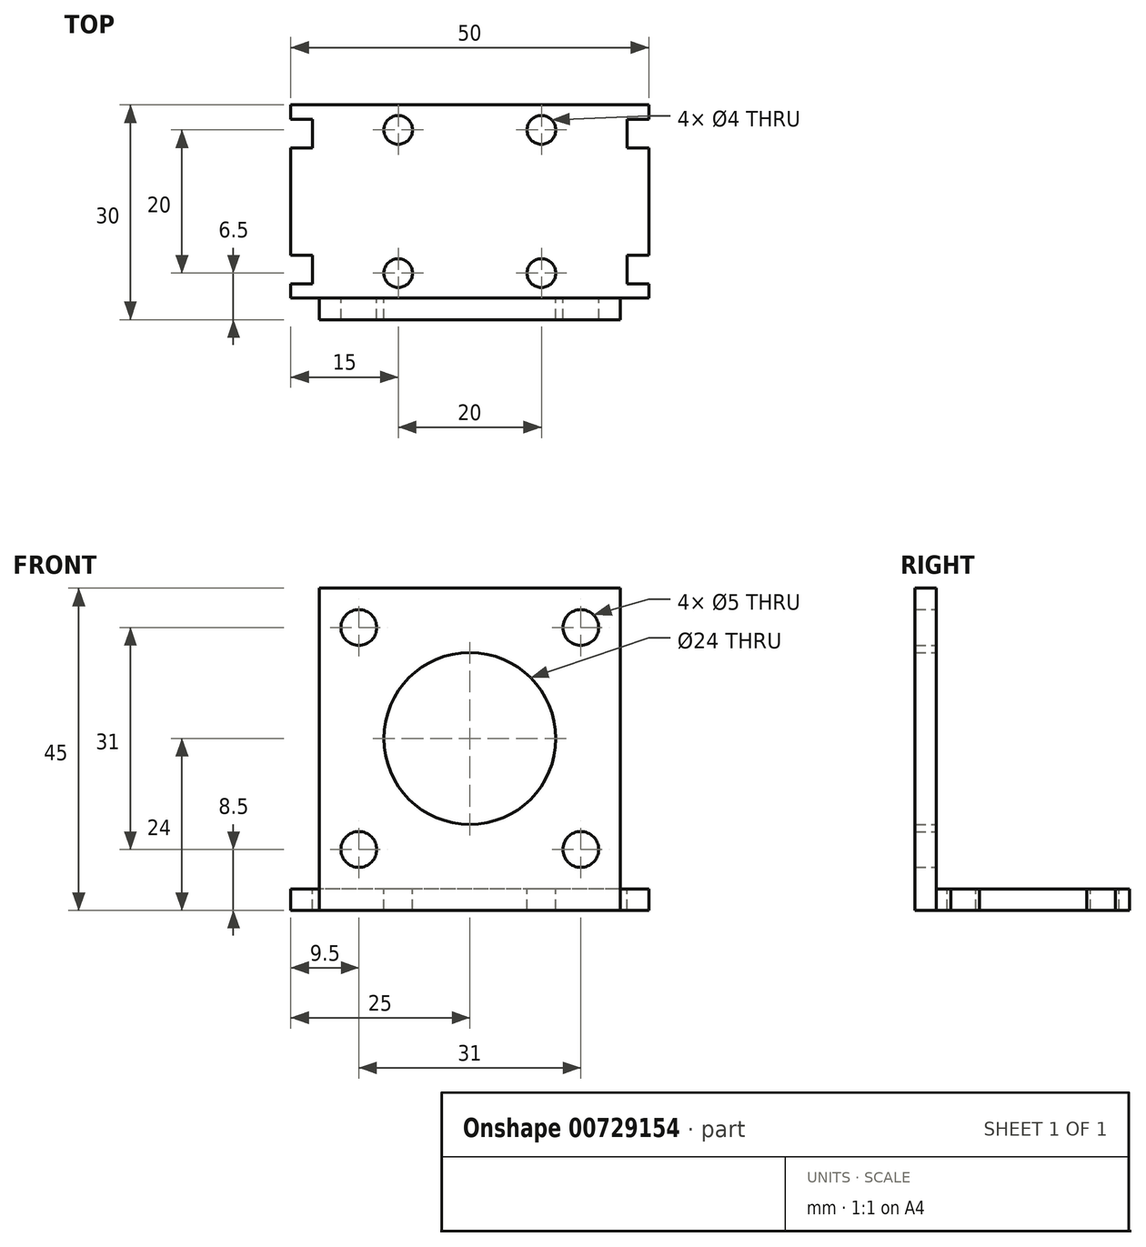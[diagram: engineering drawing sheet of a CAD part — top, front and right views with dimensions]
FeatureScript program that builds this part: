
annotation { "Feature Type Name" : "Feature", "Feature Type Description" : "" }
export const myFeature = defineFeature(function(context is Context, id is Id, definition is map)
    precondition{}
    {
        {
            var Q0;
            Q0=qCreatedBy(makeId("Top.planeOp"),FACE);
            var sketch = newSketch(context, id + "F0", { "sketchPlane" : qUnion([Q0])});
            skLineSegment(sketch, "E0.bottom", {"start": v(21, -15) * mm, "end": v(-21, -15) * mm});
            skLineSegment(sketch, "E0.top", {"start": v(21, 15) * mm, "end": v(-21, 15) * mm});
            skLineSegment(sketch, "E0.left", {"start": v(21, -15) * mm, "end": v(21, 15) * mm});
            skLineSegment(sketch, "E0.right", {"start": v(-21, -15) * mm, "end": v(-21, 15) * mm});
            skPoint(sketch, "E0.middle", {"position": v(0, 0) * mm});
            skLineSegment(sketch, "E1", {"start": v(21, -12) * mm, "end": v(-21, -12) * mm});
            skSolve(sketch);
        }
        {
            var Q0;
            {var subQ0=sQuery(id+"F0.wireOp",EDGE,"E0.top");Q0=makeQuery(id+"F0.imprint","IMPRINT",FACE,{"disambiguationData":[TD([[makeQuery(id+"F0.imprint","IMPRINT",EDGE,{"derivedFrom":subQ0}),1.0]])]});}
            extrude(context, id + "F1", {"entities" : qUnion([Q0]), "depth" : 3 * mm, "offsetDistance" : 25 * mm});
        }
        {
            var Q0;
            {var subQ0=sQuery(id+"F0.wireOp",EDGE,"E0.bottom");Q0=makeQuery(id+"F0.imprint","IMPRINT",FACE,{"disambiguationData":[TD([[makeQuery(id+"F0.imprint","IMPRINT",EDGE,{"derivedFrom":subQ0}),-1.0]])]});}
            extrude(context, id + "F2", {"entities" : qUnion([Q0]), "operationType" : NewBodyOperationType.ADD, "depth" : 45 * mm, "offsetDistance" : 25 * mm});
        }
        {
            var Q0;
            Q0=makeQuery(id+"F1.opExtrude","CAP_FACE",FACE,{"disambiguationData":[OSD([sQuery(id+"F0.wireOp",EDGE,"E0.top"),sQuery(id+"F0.wireOp",EDGE,"E0.left"),sQuery(id+"F0.wireOp",EDGE,"E0.right"),sQuery(id+"F0.wireOp",EDGE,"E1")])],"isStart":false});
            var sketch = newSketch(context, id + "F3", { "sketchPlane" : qUnion([Q0])});
            skLineSegment(sketch, "E2.bottom", {"start": v(10, -8.5) * mm, "end": v(-10, -8.5) * mm});
            skLineSegment(sketch, "E2.top", {"start": v(10, 11.5) * mm, "end": v(-10, 11.5) * mm});
            skLineSegment(sketch, "E2.left", {"start": v(10, -8.5) * mm, "end": v(10, 11.5) * mm});
            skLineSegment(sketch, "E2.right", {"start": v(-10, -8.5) * mm, "end": v(-10, 11.5) * mm});
            skSolve(sketch);
        }
        {
            var Q0;
            Q0=sQuery(id+"F3.wireOp",VERTEX,"E2.bottom.start");
            var Q1;
            Q1=sQuery(id+"F3.wireOp",VERTEX,"E2.left.end");
            var Q2;
            Q2=sQuery(id+"F3.wireOp",VERTEX,"E2.top.end");
            var Q3;
            Q3=sQuery(id+"F3.wireOp",VERTEX,"E2.right.start");
            var Q4;
            Q4=makeQuery(id+"F1.opExtrude","SWEPT_BODY",BODY,{"disambiguationData":[OSD([sQuery(id+"F0.wireOp",EDGE,"E0.top"),sQuery(id+"F0.wireOp",EDGE,"E0.left"),sQuery(id+"F0.wireOp",EDGE,"E0.right"),sQuery(id+"F0.wireOp",EDGE,"E1")])]});
            hole(context, id + "F4", {"style" : HoleStyle.SIMPLE, "endStyle" : HoleEndStyle.THROUGH, "holeDiameter" : 4 * mm, "majorDiameter" : 5 * mm, "isTappedThrough" : true, "tappedDepth" : 12 * mm, "tapClearance" : 3, "locations" : qUnion([Q0, Q1, Q2, Q3]), "scope" : qUnion([Q4])});
        }
        {
            var Q0;
            Q0=makeQuery(id+"F2.opExtrude","SWEPT_FACE",FACE,{"disambiguationData":[OSD([sQuery(id+"F0.wireOp",EDGE,"E1")])]});
            var sketch = newSketch(context, id + "F5", { "sketchPlane" : qUnion([Q0])});
            skLineSegment(sketch, "E3.bottom", {"start": v(15.5, 8.5) * mm, "end": v(-15.5, 8.5) * mm});
            skLineSegment(sketch, "E3.top", {"start": v(15.5, 39.5) * mm, "end": v(-15.5, 39.5) * mm});
            skLineSegment(sketch, "E3.left", {"start": v(15.5, 8.5) * mm, "end": v(15.5, 39.5) * mm});
            skLineSegment(sketch, "E3.right", {"start": v(-15.5, 8.5) * mm, "end": v(-15.5, 39.5) * mm});
            skPoint(sketch, "E3.middle", {"position": v(0, 24) * mm});
            skPoint(sketch, "E3.middle.positionSnap0", {"position": v(-21, 24) * mm});
            skPoint(sketch, "E3.centerSnap0", {"position": v(-21, 24) * mm});
            skSolve(sketch);
        }
        {
            var Q0;
            Q0=sQuery(id+"F5.wireOp",VERTEX,"E3.top.end");
            var Q1;
            Q1=sQuery(id+"F5.wireOp",VERTEX,"E3.bottom.end");
            var Q2;
            Q2=sQuery(id+"F5.wireOp",VERTEX,"E3.left.start");
            var Q3;
            Q3=sQuery(id+"F5.wireOp",VERTEX,"E3.top.start");
            var Q4;
            Q4=makeQuery(id+"F1.opExtrude","SWEPT_BODY",BODY,{"disambiguationData":[OSD([sQuery(id+"F0.wireOp",EDGE,"E0.top"),sQuery(id+"F0.wireOp",EDGE,"E0.left"),sQuery(id+"F0.wireOp",EDGE,"E0.right"),sQuery(id+"F0.wireOp",EDGE,"E1")])]});
            hole(context, id + "F6", {"style" : HoleStyle.SIMPLE, "endStyle" : HoleEndStyle.THROUGH, "holeDiameter" : 5 * mm, "majorDiameter" : 5 * mm, "isTappedThrough" : true, "tappedDepth" : 12 * mm, "tapClearance" : 3, "locations" : qUnion([Q0, Q1, Q2, Q3]), "scope" : qUnion([Q4])});
        }
        {
            var Q0;
            Q0=makeQuery(id+"F2.opExtrude","SWEPT_FACE",FACE,{"disambiguationData":[OSD([sQuery(id+"F0.wireOp",EDGE,"E1")])]});
            var sketch = newSketch(context, id + "F7", { "sketchPlane" : qUnion([Q0])});
            skCircle(sketch, "E4", {"center": v(0, 24) * mm, "radius": 12 * mm});
            skPoint(sketch, "E4.centerSnap0", {"position": v(0, 45) * mm});
            skPoint(sketch, "E4.centerSnap1", {"position": v(-21, 24) * mm});
            skSolve(sketch);
        }
        {
            var Q0;
            Q0=makeQuery(id+"F7.imprint","IMPRINT",FACE,{"disambiguationData":[TD([[makeQuery(id+"F7.imprint","IMPRINT",EDGE,{"derivedFrom":sQuery(id+"F7.wireOp",EDGE,"E4")}),1.0]])]});
            extrude(context, id + "F8", {"entities" : qUnion([Q0]), "operationType" : NewBodyOperationType.REMOVE, "oppositeDirection" : true, "depth" : 25 * mm, "offsetDistance" : 25 * mm});
        }
        {
            var Q0;
            {var subQ0=sQuery(id+"F0.wireOp",EDGE,"E0.right");Q0=makeQuery(id+"F2.boolean.opBoolean","MERGE",FACE,{"derivedFrom":[makeQuery(id+"F1.opExtrude","SWEPT_FACE",FACE,{"disambiguationData":[OSD([subQ0])]}),makeQuery(id+"F2.opExtrude","SWEPT_FACE",FACE,{"disambiguationData":[OSD([subQ0])]})]});}
            var sketch = newSketch(context, id + "F9", { "sketchPlane" : qUnion([Q0])});
            skPoint(sketch, "E5.oppositeSnap0", {"position": v(0, 0) * mm});
            skLineSegment(sketch, "E5.bottom", {"start": v(-15, 3) * mm, "end": v(12, 3) * mm});
            skLineSegment(sketch, "E5.top", {"start": v(-15, 0) * mm, "end": v(12, 0) * mm});
            skLineSegment(sketch, "E5.left", {"start": v(-15, 3) * mm, "end": v(-15, 0) * mm});
            skLineSegment(sketch, "E5.right", {"start": v(12, 3) * mm, "end": v(12, 0) * mm});
            skSolve(sketch);
        }
        {
            var Q0;
            Q0=makeQuery(id+"F9.imprint","IMPRINT",FACE,{"disambiguationData":[TD([[makeQuery(id+"F9.imprint","IMPRINT",EDGE,{"derivedFrom":sQuery(id+"F9.wireOp",EDGE,"E5.bottom")}),1.0]])]});
            extrude(context, id + "F10", {"entities" : qUnion([Q0]), "operationType" : NewBodyOperationType.ADD, "depth" : 4 * mm, "offsetDistance" : 25 * mm});
        }
        {
            var Q0;
            Q0=makeQuery(id+"F10.boolean.opBoolean","MERGE",FACE,{"derivedFrom":[makeQuery(id+"F1.opExtrude","CAP_FACE",FACE,{"disambiguationData":[OSD([sQuery(id+"F0.wireOp",EDGE,"E0.top"),sQuery(id+"F0.wireOp",EDGE,"E0.left"),sQuery(id+"F0.wireOp",EDGE,"E0.right"),sQuery(id+"F0.wireOp",EDGE,"E1")])],"isStart":false}),makeQuery(id+"F10.opExtrude","SWEPT_FACE",FACE,{"disambiguationData":[OSD([sQuery(id+"F9.wireOp",EDGE,"E5.bottom")])]})]});
            var sketch = newSketch(context, id + "F11", { "sketchPlane" : qUnion([Q0])});
            skPoint(sketch, "E6", {"position": v(-22, -6) * mm});
            skPoint(sketch, "E7", {"position": v(-22, 9) * mm});
            skLineSegment(sketch, "E8.bottom", {"start": v(-22, 9) * mm, "end": v(-25, 9) * mm});
            skLineSegment(sketch, "E8.top", {"start": v(-22, 13) * mm, "end": v(-25, 13) * mm});
            skLineSegment(sketch, "E8.left", {"start": v(-22, 9) * mm, "end": v(-22, 13) * mm});
            skLineSegment(sketch, "E8.right", {"start": v(-25, 9) * mm, "end": v(-25, 13) * mm});
            skLineSegment(sketch, "E9.bottom", {"start": v(-22, -6) * mm, "end": v(-25, -6) * mm});
            skLineSegment(sketch, "E9.top", {"start": v(-22, -10) * mm, "end": v(-25, -10) * mm});
            skLineSegment(sketch, "E9.left", {"start": v(-22, -6) * mm, "end": v(-22, -10) * mm});
            skLineSegment(sketch, "E9.right", {"start": v(-25, -6) * mm, "end": v(-25, -10) * mm});
            skSolve(sketch);
        }
        {
            var Q0;
            Q0=makeQuery(id+"F11.imprint","IMPRINT",FACE,{"disambiguationData":[TD([[makeQuery(id+"F11.imprint","IMPRINT",EDGE,{"derivedFrom":sQuery(id+"F11.wireOp",EDGE,"E8.bottom")}),-1.0]])]});
            var Q1;
            Q1=qSketchRegion(id+"F11",true);
            var Q2;
            Q2=makeQuery(id+"F11.imprint","IMPRINT",FACE,{"disambiguationData":[TD([[makeQuery(id+"F11.imprint","IMPRINT",EDGE,{"derivedFrom":sQuery(id+"F11.wireOp",EDGE,"E9.bottom")}),1.0]])]});
            extrude(context, id + "F12", {"entities" : qUnion([Q0, Q1, Q2]), "operationType" : NewBodyOperationType.REMOVE, "oppositeDirection" : true, "depth" : 25 * mm, "offsetDistance" : 25 * mm});
        }
        {
            var Q0;
            {var subQ0=sQuery(id+"F0.wireOp",EDGE,"E0.left");Q0=makeQuery(id+"F2.boolean.opBoolean","MERGE",FACE,{"derivedFrom":[makeQuery(id+"F1.opExtrude","SWEPT_FACE",FACE,{"disambiguationData":[OSD([subQ0])]}),makeQuery(id+"F2.opExtrude","SWEPT_FACE",FACE,{"disambiguationData":[OSD([subQ0])]})]});}
            var sketch = newSketch(context, id + "F13", { "sketchPlane" : qUnion([Q0])});
            skLineSegment(sketch, "E10.bottom", {"start": v(-12, 3) * mm, "end": v(15, 3) * mm});
            skLineSegment(sketch, "E10.top", {"start": v(-12, 0) * mm, "end": v(15, 0) * mm});
            skLineSegment(sketch, "E10.left", {"start": v(-12, 3) * mm, "end": v(-12, 0) * mm});
            skLineSegment(sketch, "E10.right", {"start": v(15, 3) * mm, "end": v(15, 0) * mm});
            skSolve(sketch);
        }
        {
            var Q0;
            Q0=qSketchRegion(id+"F13",true);
            extrude(context, id + "F14", {"entities" : qUnion([Q0]), "operationType" : NewBodyOperationType.ADD, "depth" : 4 * mm, "offsetDistance" : 25 * mm});
        }
        {
            var Q0;
            Q0=makeQuery(id+"F14.boolean.opBoolean","MERGE",FACE,{"derivedFrom":[makeQuery(id+"F10.boolean.opBoolean","MERGE",FACE,{"derivedFrom":[makeQuery(id+"F1.opExtrude","CAP_FACE",FACE,{"disambiguationData":[OSD([sQuery(id+"F0.wireOp",EDGE,"E0.top"),sQuery(id+"F0.wireOp",EDGE,"E0.left"),sQuery(id+"F0.wireOp",EDGE,"E0.right"),sQuery(id+"F0.wireOp",EDGE,"E1")])],"isStart":false}),makeQuery(id+"F10.opExtrude","SWEPT_FACE",FACE,{"disambiguationData":[OSD([sQuery(id+"F9.wireOp",EDGE,"E5.bottom")])]})]}),makeQuery(id+"F14.opExtrude","SWEPT_FACE",FACE,{"disambiguationData":[OSD([sQuery(id+"F13.wireOp",EDGE,"E10.bottom")])]})]});
            var sketch = newSketch(context, id + "F15", { "sketchPlane" : qUnion([Q0])});
            skLineSegment(sketch, "E11.bottom", {"start": v(25, 9) * mm, "end": v(22, 9) * mm});
            skLineSegment(sketch, "E11.top", {"start": v(25, 13) * mm, "end": v(22, 13) * mm});
            skLineSegment(sketch, "E11.left", {"start": v(25, 9) * mm, "end": v(25, 13) * mm});
            skLineSegment(sketch, "E11.right", {"start": v(22, 9) * mm, "end": v(22, 13) * mm});
            skLineSegment(sketch, "E12.bottom", {"start": v(25, -6) * mm, "end": v(22, -6) * mm});
            skLineSegment(sketch, "E12.top", {"start": v(25, -10) * mm, "end": v(22, -10) * mm});
            skLineSegment(sketch, "E12.left", {"start": v(25, -6) * mm, "end": v(25, -10) * mm});
            skLineSegment(sketch, "E12.right", {"start": v(22, -6) * mm, "end": v(22, -10) * mm});
            skSolve(sketch);
        }
        {
            var Q0;
            Q0=makeQuery(id+"F15.imprint","IMPRINT",FACE,{"disambiguationData":[TD([[makeQuery(id+"F15.imprint","IMPRINT",EDGE,{"derivedFrom":sQuery(id+"F15.wireOp",EDGE,"E11.bottom")}),-1.0]])]});
            var Q1;
            Q1=makeQuery(id+"F15.imprint","IMPRINT",FACE,{"disambiguationData":[TD([[makeQuery(id+"F15.imprint","IMPRINT",EDGE,{"derivedFrom":sQuery(id+"F15.wireOp",EDGE,"E12.bottom")}),1.0]])]});
            extrude(context, id + "F16", {"entities" : qUnion([Q0, Q1]), "operationType" : NewBodyOperationType.REMOVE, "oppositeDirection" : true, "depth" : 25 * mm, "offsetDistance" : 25 * mm});
        }
    });
